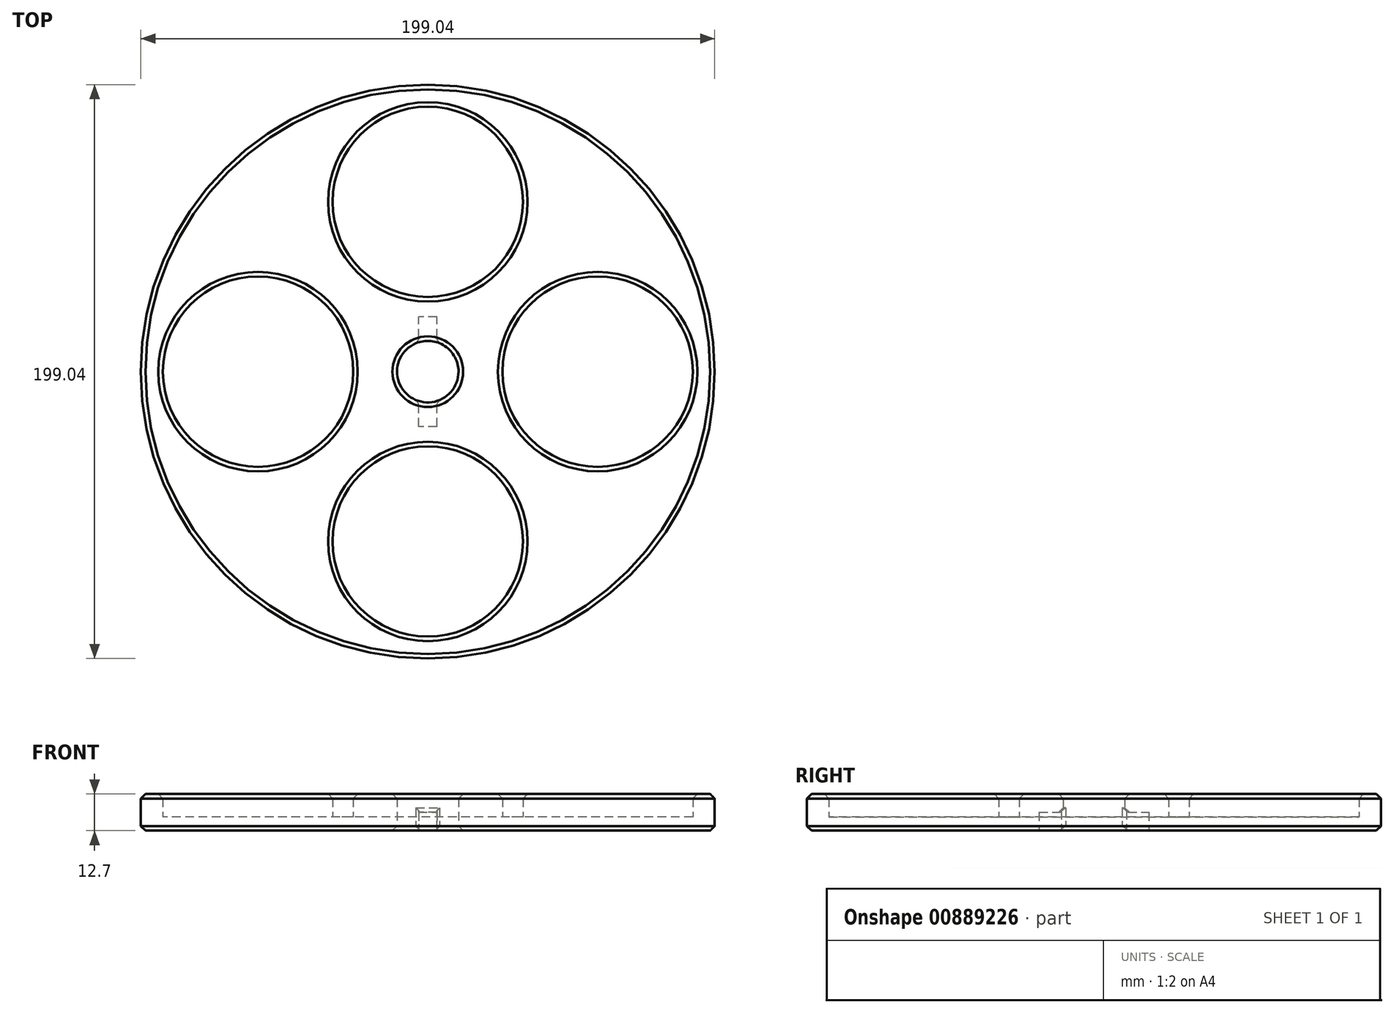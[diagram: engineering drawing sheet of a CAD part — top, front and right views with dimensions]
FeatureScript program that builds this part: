
annotation { "Feature Type Name" : "Feature", "Feature Type Description" : "" }
export const myFeature = defineFeature(function(context is Context, id is Id, definition is map)
    precondition{}
    {
        {
            var Q0;
            Q0=qCreatedBy(makeId("Top.planeOp"),FACE);
            var sketch = newSketch(context, id + "F0", { "sketchPlane" : qUnion([Q0])});
            skCircle(sketch, "E0", {"center": v(0, 0) * mm, "radius": 10.67 * mm});
            skCircle(sketch, "E1", {"center": v(0, 0) * mm, "radius": 7.9 * mm});
            skCircle(sketch, "E2", {"center": v(0, 0) * mm, "radius": 18.28 * mm, "construction": true});
            skCircle(sketch, "E3", {"center": v(0, 58.9) * mm, "radius": 40.62 * mm, "construction": true});
            skCircle(sketch, "E4", {"center": v(0, 58.9) * mm, "radius": 33 * mm});
            skCircle(sketch, "E5.1.0", {"center": v(-58.9, 0) * mm, "radius": 33 * mm});
            skCircle(sketch, "E5.2.0", {"center": v(0, -58.9) * mm, "radius": 33 * mm});
            skCircle(sketch, "E6.1.3.0", {"center": v(58.9, 0) * mm, "radius": 33 * mm});
            skCircle(sketch, "E7", {"center": v(58.9, 0) * mm, "radius": 40.62 * mm, "construction": true});
            skCircle(sketch, "E8", {"center": v(0, -58.9) * mm, "radius": 40.62 * mm, "construction": true});
            skCircle(sketch, "E9", {"center": v(-58.9, 0) * mm, "radius": 40.62 * mm, "construction": true});
            skCircle(sketch, "E10", {"center": v(0, 0) * mm, "radius": 109.54 * mm});
            skCircle(sketch, "E11", {"center": v(0, 0) * mm, "radius": 101.1 * mm});
            skLineSegment(sketch, "E12", {"start": v(0, 10.67) * mm, "end": v(0, 18.28) * mm, "construction": true});
            skLineSegment(sketch, "E13", {"start": v(0, 91.9) * mm, "end": v(0, 99.52) * mm, "construction": true});
            skCircle(sketch, "E14", {"center": v(0, 0) * mm, "radius": 99.52 * mm});
            skSolve(sketch);
        }
        {
            var Q0;
            Q0=makeQuery(id+"F0.imprint","IMPRINT",FACE,{"disambiguationData":[TD([[makeQuery(id+"F0.imprint","IMPRINT",EDGE,{"derivedFrom":sQuery(id+"F0.wireOp",EDGE,"E0")}),-1.0]])]});
            extrude(context, id + "F1", {"entities" : qUnion([Q0]), "depth" : 12.7 * mm, "offsetDistance" : 25.4 * mm});
        }
        {
            var Q0;
            Q0=makeQuery(id+"F0.imprint","IMPRINT",FACE,{"disambiguationData":[TD([[makeQuery(id+"F0.imprint","IMPRINT",EDGE,{"derivedFrom":sQuery(id+"F0.wireOp",EDGE,"E0")}),-1.0]])]});
            var Q1;
            Q1=makeQuery(id+"F0.imprint","IMPRINT",FACE,{"disambiguationData":[TD([[makeQuery(id+"F0.imprint","IMPRINT",EDGE,{"derivedFrom":sQuery(id+"F0.wireOp",EDGE,"E6.1.3.0")}),1.0]])]});
            var Q2;
            Q2=makeQuery(id+"F0.imprint","IMPRINT",FACE,{"disambiguationData":[TD([[makeQuery(id+"F0.imprint","IMPRINT",EDGE,{"derivedFrom":sQuery(id+"F0.wireOp",EDGE,"E5.2.0")}),1.0]])]});
            var Q3;
            Q3=makeQuery(id+"F0.imprint","IMPRINT",FACE,{"disambiguationData":[TD([[makeQuery(id+"F0.imprint","IMPRINT",EDGE,{"derivedFrom":sQuery(id+"F0.wireOp",EDGE,"E5.1.0")}),1.0]])]});
            var Q4;
            Q4=makeQuery(id+"F0.imprint","IMPRINT",FACE,{"disambiguationData":[TD([[makeQuery(id+"F0.imprint","IMPRINT",EDGE,{"derivedFrom":sQuery(id+"F0.wireOp",EDGE,"E4")}),1.0]])]});
            extrude(context, id + "F2", {"entities" : qUnion([Q0, Q1, Q2, Q3, Q4]), "operationType" : NewBodyOperationType.ADD, "depth" : 4.76 * mm, "offsetDistance" : 25.4 * mm});
        }
        {
            var Q0;
            {var subQ0=sQuery(id+"F0.wireOp",EDGE,"E14");var subQ1=sQuery(id+"F0.wireOp",EDGE,"E0");Q0=makeQuery(id+"F2.boolean.opBoolean","MERGE",FACE,{"derivedFrom":[makeQuery(id+"F1.opExtrude","CAP_FACE",FACE,{"disambiguationData":[OSD([subQ1,sQuery(id+"F0.wireOp",EDGE,"E4"),sQuery(id+"F0.wireOp",EDGE,"E5.1.0"),sQuery(id+"F0.wireOp",EDGE,"E5.2.0"),sQuery(id+"F0.wireOp",EDGE,"E6.1.3.0"),subQ0])],"isStart":true}),makeQuery(id+"F2.opExtrude","CAP_FACE",FACE,{"disambiguationData":[OSD([subQ1,subQ0])],"isStart":true})]});}
            var sketch = newSketch(context, id + "F3", { "sketchPlane" : qUnion([Q0])});
            skLineSegment(sketch, "E15.bottom", {"start": v(3.18, 19.05) * mm, "end": v(-3.17, 19.05) * mm});
            skLineSegment(sketch, "E15.top", {"start": v(3.17, -19.05) * mm, "end": v(-3.18, -19.05) * mm});
            skLineSegment(sketch, "E15.left", {"start": v(3.18, 19.05) * mm, "end": v(3.18, -19.05) * mm});
            skLineSegment(sketch, "E15.right", {"start": v(-3.17, 19.05) * mm, "end": v(-3.18, -19.05) * mm});
            skPoint(sketch, "E15.middle", {"position": v(0, 0) * mm});
            skSolve(sketch);
        }
        {
            var Q0;
            {var subQ0=sQuery(id+"F3.wireOp",EDGE,"E15.left");var subQ1=sQuery(id+"F0.wireOp",EDGE,"E14");var subQ2=sQuery(id+"F0.wireOp",EDGE,"E0");var subQ3=makeQuery(id+"F5.opChamfer","BLEND_EDGE",EDGE,{"blendedFrom":[makeQuery(id+"F1.opExtrude","CAP_EDGE",EDGE,{"disambiguationData":[OSD([subQ2])],"isStart":true}),makeQuery(id+"F2.boolean.opBoolean","MERGE",FACE,{"derivedFrom":[makeQuery(id+"F1.opExtrude","CAP_FACE",FACE,{"disambiguationData":[OSD([subQ2,sQuery(id+"F0.wireOp",EDGE,"E4"),sQuery(id+"F0.wireOp",EDGE,"E5.1.0"),sQuery(id+"F0.wireOp",EDGE,"E5.2.0"),sQuery(id+"F0.wireOp",EDGE,"E6.1.3.0"),subQ1])],"isStart":true}),makeQuery(id+"F2.opExtrude","CAP_FACE",FACE,{"disambiguationData":[OSD([subQ2,subQ1])],"isStart":true})]})],"blendedInto":[makeQuery(id+"F2.boolean.opBoolean","MERGE",FACE,{"derivedFrom":[makeQuery(id+"F1.opExtrude","CAP_FACE",FACE,{"disambiguationData":[OSD([subQ2,sQuery(id+"F0.wireOp",EDGE,"E4"),sQuery(id+"F0.wireOp",EDGE,"E5.1.0"),sQuery(id+"F0.wireOp",EDGE,"E5.2.0"),sQuery(id+"F0.wireOp",EDGE,"E6.1.3.0"),subQ1])],"isStart":true}),makeQuery(id+"F2.opExtrude","CAP_FACE",FACE,{"disambiguationData":[OSD([subQ2,subQ1])],"isStart":true})]})]});var subQ4=makeQuery(id+"F3.imprint","INTERSECT",VERTEX,{"disambiguationData":[OD(0.0)],"derivedFrom":[subQ3,subQ0]});Q0=makeQuery(id+"F3.imprint","IMPRINT",FACE,{"disambiguationData":[TD([[makeQuery(id+"F3.imprint","IMPRINT",EDGE,{"disambiguationData":[TD([[subQ4,-1.0]])],"derivedFrom":subQ0}),-1.0]])]});}
            var Q1;
            {var subQ0=sQuery(id+"F3.wireOp",EDGE,"E15.bottom");Q1=makeQuery(id+"F3.imprint","IMPRINT",FACE,{"disambiguationData":[TD([[makeQuery(id+"F3.imprint","IMPRINT",EDGE,{"derivedFrom":subQ0}),1.0]])]});}
            var Q2;
            {var subQ0=sQuery(id+"F3.wireOp",EDGE,"E15.top");Q2=makeQuery(id+"F3.imprint","IMPRINT",FACE,{"disambiguationData":[TD([[makeQuery(id+"F3.imprint","IMPRINT",EDGE,{"derivedFrom":subQ0}),-1.0]])]});}
            extrude(context, id + "F4", {"entities" : qUnion([Q0, Q1, Q2]), "operationType" : NewBodyOperationType.REMOVE, "oppositeDirection" : true, "depth" : 6.35 * mm, "offsetDistance" : 25.4 * mm});
        }
        {
            var Q0;
            Q0=makeQuery(id+"F1.opExtrude","CAP_EDGE",EDGE,{"disambiguationData":[OSD([sQuery(id+"F0.wireOp",EDGE,"E14")])],"isStart":false});
            var Q1;
            Q1=makeQuery(id+"F1.opExtrude","CAP_EDGE",EDGE,{"disambiguationData":[OSD([sQuery(id+"F0.wireOp",EDGE,"E14")])],"isStart":true});
            var Q2;
            Q2=makeQuery(id+"F1.opExtrude","CAP_EDGE",EDGE,{"disambiguationData":[OSD([sQuery(id+"F0.wireOp",EDGE,"E0")])],"isStart":false});
            var Q3;
            Q3=makeQuery(id+"F1.opExtrude","CAP_EDGE",EDGE,{"disambiguationData":[OSD([sQuery(id+"F0.wireOp",EDGE,"E0")])],"isStart":true});
            var Q4;
            Q4=makeQuery(id+"F1.opExtrude","CAP_EDGE",EDGE,{"disambiguationData":[OSD([sQuery(id+"F0.wireOp",EDGE,"E5.1.0")])],"isStart":false});
            var Q5;
            Q5=makeQuery(id+"F1.opExtrude","CAP_EDGE",EDGE,{"disambiguationData":[OSD([sQuery(id+"F0.wireOp",EDGE,"E5.2.0")])],"isStart":false});
            var Q6;
            Q6=makeQuery(id+"F1.opExtrude","CAP_EDGE",EDGE,{"disambiguationData":[OSD([sQuery(id+"F0.wireOp",EDGE,"E4")])],"isStart":false});
            var Q7;
            Q7=makeQuery(id+"F1.opExtrude","CAP_EDGE",EDGE,{"disambiguationData":[OSD([sQuery(id+"F0.wireOp",EDGE,"E6.1.3.0")])],"isStart":false});
            var Q8;
            {var subQ2=sQuery(id+"F3.wireOp",EDGE,"E15.right");Q8=makeQuery(id+"F4.boolean.opBoolean","COPY",EDGE,{"disambiguationData":[TD([makeQuery(id+"F4.opExtrude","SWEPT_FACE",FACE,{"disambiguationData":[OSD([sQuery(id+"F3.wireOp",EDGE,"E15.bottom")])]})])],"derivedFrom":makeQuery(id+"F4.opExtrude","CAP_EDGE",EDGE,{"disambiguationData":[OSD([subQ2])],"isStart":true})});}
            var Q9;
            Q9=makeQuery(id+"F4.boolean.opBoolean","COPY",EDGE,{"derivedFrom":makeQuery(id+"F4.opExtrude","CAP_EDGE",EDGE,{"disambiguationData":[OSD([sQuery(id+"F3.wireOp",EDGE,"E15.bottom")])],"isStart":true})});
            var Q10;
            {var subQ2=sQuery(id+"F3.wireOp",EDGE,"E15.left");Q10=makeQuery(id+"F4.boolean.opBoolean","COPY",EDGE,{"disambiguationData":[TD([makeQuery(id+"F4.opExtrude","SWEPT_FACE",FACE,{"disambiguationData":[OSD([sQuery(id+"F3.wireOp",EDGE,"E15.bottom")])]})])],"derivedFrom":makeQuery(id+"F4.opExtrude","CAP_EDGE",EDGE,{"disambiguationData":[OSD([subQ2])],"isStart":true})});}
            var Q11;
            {var subQ2=sQuery(id+"F3.wireOp",EDGE,"E15.right");Q11=makeQuery(id+"F4.boolean.opBoolean","COPY",EDGE,{"disambiguationData":[TD([makeQuery(id+"F4.opExtrude","SWEPT_FACE",FACE,{"disambiguationData":[OSD([sQuery(id+"F3.wireOp",EDGE,"E15.top")])]})])],"derivedFrom":makeQuery(id+"F4.opExtrude","CAP_EDGE",EDGE,{"disambiguationData":[OSD([subQ2])],"isStart":true})});}
            var Q12;
            Q12=makeQuery(id+"F4.boolean.opBoolean","COPY",EDGE,{"derivedFrom":makeQuery(id+"F4.opExtrude","CAP_EDGE",EDGE,{"disambiguationData":[OSD([sQuery(id+"F3.wireOp",EDGE,"E15.top")])],"isStart":true})});
            var Q13;
            {var subQ2=sQuery(id+"F3.wireOp",EDGE,"E15.left");Q13=makeQuery(id+"F4.boolean.opBoolean","COPY",EDGE,{"disambiguationData":[TD([makeQuery(id+"F4.opExtrude","SWEPT_FACE",FACE,{"disambiguationData":[OSD([sQuery(id+"F3.wireOp",EDGE,"E15.top")])]})])],"derivedFrom":makeQuery(id+"F4.opExtrude","CAP_EDGE",EDGE,{"disambiguationData":[OSD([subQ2])],"isStart":true})});}
            var Q14;
            Q14=makeQuery(id+"F4.boolean.opBoolean","INTERSECT",EDGE,{"disambiguationData":[OD(1.0)],"derivedFrom":[makeQuery(id+"F1.opExtrude","SWEPT_FACE",FACE,{"disambiguationData":[OSD([sQuery(id+"F0.wireOp",EDGE,"E0")])]}),makeQuery(id+"F4.opExtrude","CAP_FACE",FACE,{"disambiguationData":[OSD([sQuery(id+"F3.wireOp",EDGE,"E15.bottom"),sQuery(id+"F3.wireOp",EDGE,"E15.top"),sQuery(id+"F3.wireOp",EDGE,"E15.left"),sQuery(id+"F3.wireOp",EDGE,"E15.right")])],"isStart":false})]});
            var Q15;
            Q15=makeQuery(id+"F4.boolean.opBoolean","INTERSECT",EDGE,{"disambiguationData":[OD(1.0)],"derivedFrom":[makeQuery(id+"F1.opExtrude","SWEPT_FACE",FACE,{"disambiguationData":[OSD([sQuery(id+"F0.wireOp",EDGE,"E0")])]}),makeQuery(id+"F4.opExtrude","SWEPT_FACE",FACE,{"disambiguationData":[OSD([sQuery(id+"F3.wireOp",EDGE,"E15.left")])]})]});
            var Q16;
            Q16=makeQuery(id+"F4.boolean.opBoolean","INTERSECT",EDGE,{"disambiguationData":[OD(1.0)],"derivedFrom":[makeQuery(id+"F1.opExtrude","SWEPT_FACE",FACE,{"disambiguationData":[OSD([sQuery(id+"F0.wireOp",EDGE,"E0")])]}),makeQuery(id+"F4.opExtrude","SWEPT_FACE",FACE,{"disambiguationData":[OSD([sQuery(id+"F3.wireOp",EDGE,"E15.right")])]})]});
            var Q17;
            Q17=makeQuery(id+"F4.boolean.opBoolean","INTERSECT",EDGE,{"disambiguationData":[OD(0.0)],"derivedFrom":[makeQuery(id+"F1.opExtrude","SWEPT_FACE",FACE,{"disambiguationData":[OSD([sQuery(id+"F0.wireOp",EDGE,"E0")])]}),makeQuery(id+"F4.opExtrude","CAP_FACE",FACE,{"disambiguationData":[OSD([sQuery(id+"F3.wireOp",EDGE,"E15.bottom"),sQuery(id+"F3.wireOp",EDGE,"E15.top"),sQuery(id+"F3.wireOp",EDGE,"E15.left"),sQuery(id+"F3.wireOp",EDGE,"E15.right")])],"isStart":false})]});
            var Q18;
            Q18=makeQuery(id+"F4.boolean.opBoolean","INTERSECT",EDGE,{"disambiguationData":[OD(0.0)],"derivedFrom":[makeQuery(id+"F1.opExtrude","SWEPT_FACE",FACE,{"disambiguationData":[OSD([sQuery(id+"F0.wireOp",EDGE,"E0")])]}),makeQuery(id+"F4.opExtrude","SWEPT_FACE",FACE,{"disambiguationData":[OSD([sQuery(id+"F3.wireOp",EDGE,"E15.right")])]})]});
            var Q19;
            Q19=makeQuery(id+"F4.boolean.opBoolean","INTERSECT",EDGE,{"disambiguationData":[OD(0.0)],"derivedFrom":[makeQuery(id+"F1.opExtrude","SWEPT_FACE",FACE,{"disambiguationData":[OSD([sQuery(id+"F0.wireOp",EDGE,"E0")])]}),makeQuery(id+"F4.opExtrude","SWEPT_FACE",FACE,{"disambiguationData":[OSD([sQuery(id+"F3.wireOp",EDGE,"E15.left")])]})]});
            chamfer(context, id + "F5", {"entities" : qUnion([Q0, Q1, Q2, Q3, Q4, Q5, Q6, Q7, Q8, Q9, Q10, Q11, Q12, Q13, Q14, Q15, Q16, Q17, Q18, Q19]), "width" : 1.59 * mm, "tangentPropagation" : true});
        }
    });
